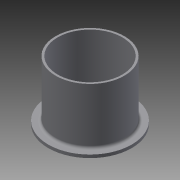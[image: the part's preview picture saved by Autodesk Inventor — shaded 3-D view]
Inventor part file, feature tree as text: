
AUTODESK INVENTOR PART (.ipt)
format: ipt  version: 2014 (Build 180170000, 170)  size: 101,888 bytes
history: native  units: in
note: dims shown in document units (in); Inventor stores cm internally (conversion verified against a paired STEP export)
features: revolve x1, fillet x1, sketch x1, reference x1
ambient origin geometry x8: Origin, YZ Plane, XZ Plane, XY Plane, X Axis, Y Axis, Z Axis, Center Point
bodies: Solid1 (feature_tree)
feature tree (4):
  revolve  "Revolution1"  [1 undecoded]
  fillet  "Fillet1"  [1 undecoded]
  sketch  "Sketch1"  dims[d0=0.1in d1=0.03in d2=90.0deg d3=0.025in d4=0.02in d5=0.3175in d6=0.31in]
  reference  "Reference1"
note: 2 required parameter values undecoded (feature->parameter linkage not recoverable at this tier; creation-order binding heuristic only, values carry confidence <= 0.55)